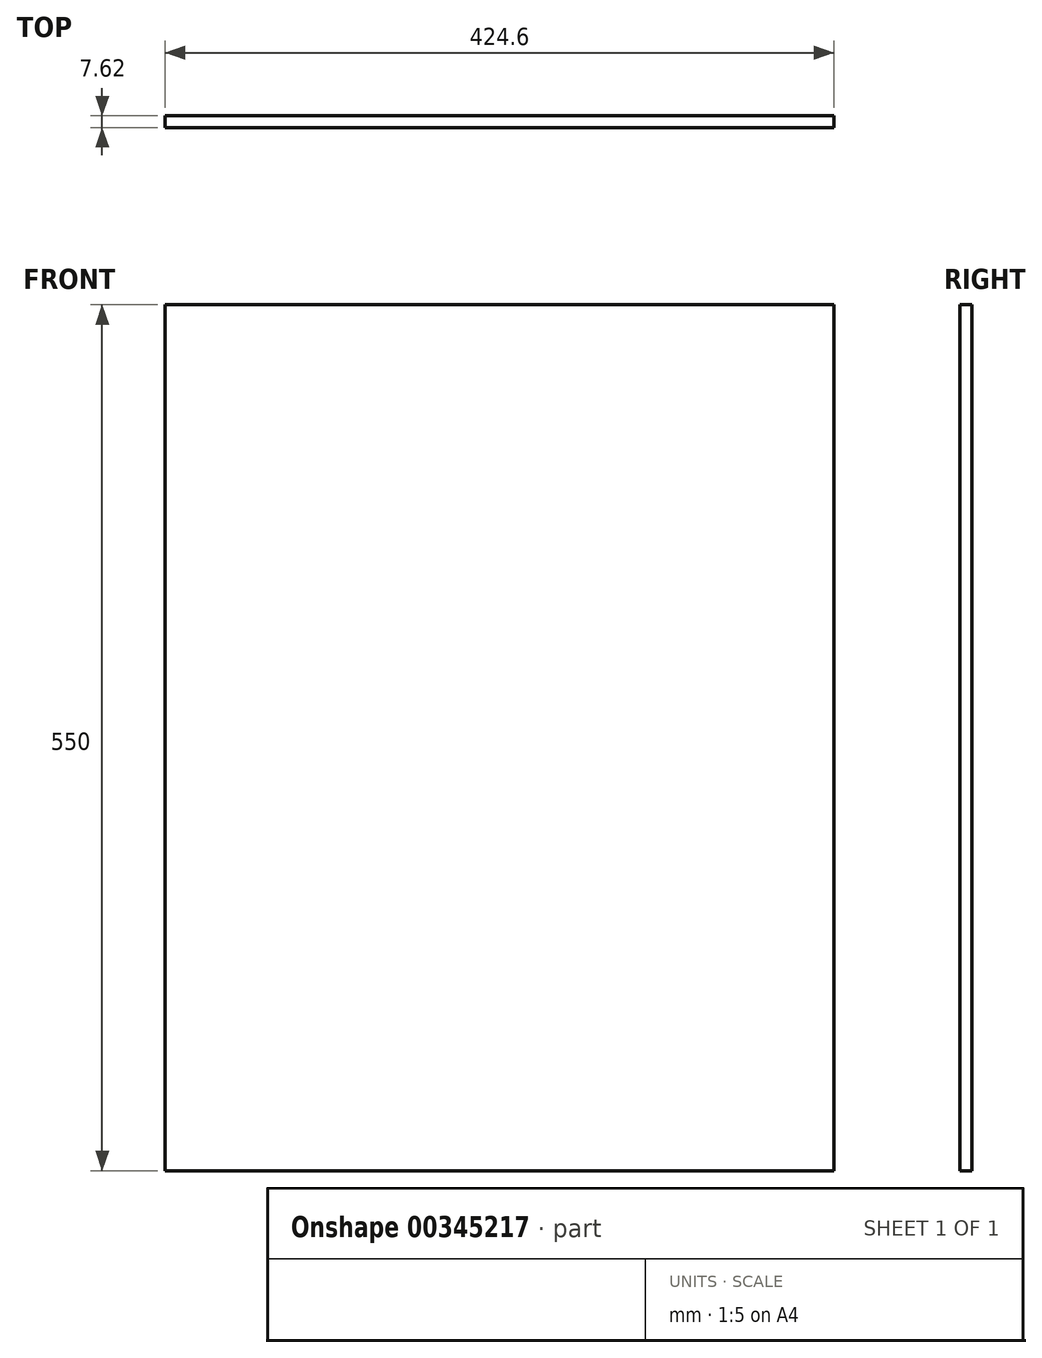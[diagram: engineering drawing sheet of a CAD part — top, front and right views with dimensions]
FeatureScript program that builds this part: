
annotation { "Feature Type Name" : "Feature", "Feature Type Description" : "" }
export const myFeature = defineFeature(function(context is Context, id is Id, definition is map)
    precondition{}
    {
        {
            var Q0;
            Q0=qCreatedBy(makeId("Front.planeOp"),FACE);
            var sketch = newSketch(context, id + "F0", { "sketchPlane" : qUnion([Q0])});
            skLineSegment(sketch, "E0.bottom", {"start": v(-214.18, 359.84) * mm, "end": v(210.42, 359.84) * mm});
            skLineSegment(sketch, "E0.top", {"start": v(-214.18, -190.16) * mm, "end": v(210.42, -190.16) * mm});
            skLineSegment(sketch, "E0.left", {"start": v(-214.18, 359.84) * mm, "end": v(-214.18, -190.16) * mm});
            skLineSegment(sketch, "E0.right", {"start": v(210.42, 359.84) * mm, "end": v(210.42, -190.16) * mm});
            skSolve(sketch);
        }
        {
            var Q0;
            Q0=makeQuery(id+"F0.imprint","IMPRINT",FACE,{"disambiguationData":[TD([[makeQuery(id+"F0.imprint","IMPRINT",EDGE,{"derivedFrom":sQuery(id+"F0.wireOp",EDGE,"E0.bottom")}),-1.0]])]});
            extrude(context, id + "F1", {"entities" : qUnion([Q0]), "depth" : 7.62 * mm});
        }
    });
